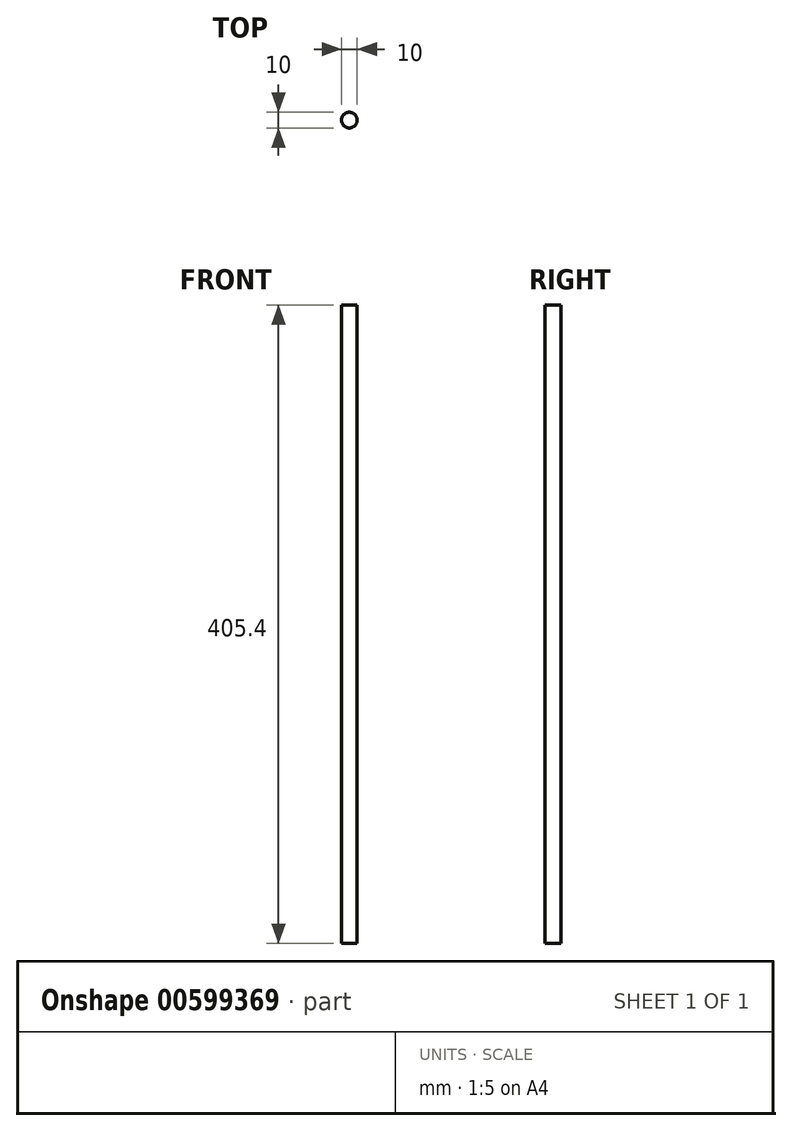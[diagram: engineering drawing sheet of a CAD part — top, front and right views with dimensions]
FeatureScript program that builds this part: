
annotation { "Feature Type Name" : "Feature", "Feature Type Description" : "" }
export const myFeature = defineFeature(function(context is Context, id is Id, definition is map)
    precondition{}
    {
        {
            var Q0;
            Q0=qCreatedBy(makeId("Top.planeOp"),FACE);
            var sketch = newSketch(context, id + "F0", { "sketchPlane" : qUnion([Q0])});
            skCircle(sketch, "E0", {"center": v(0, 0) * mm, "radius": 5 * mm});
            skSolve(sketch);
        }
        {
            var Q0;
            Q0=qSketchRegion(id+"F0",true);
            extrude(context, id + "F1", {"entities" : qUnion([Q0]), "depth" : 405.4 * mm});
        }
    });
